# Revit family: НЕВАТОМ_Вентилятор ВР 280-46, Версия 2
name_source: partatom
category: Оборудование
revit_build: Autodesk Revit 2017 (Build: 20170118_1100(x64)
units: mm (PartAtom-declared; Revit-internal decimal feet)

## family parameters
Всегда вертикально = Да
На основе рабочей плоскости = Нет
Общий = Да
При загрузке вырезать с полостями = Нет
Размер круглого соединителя = Использовать диаметр
Тип детали = Нормальный
Точка расчета площади = Нет

## types (7) — shared parameters
ADSK_Количество = 1
ADSK_Количество фаз = 3
ADSK_Количество фаз числовое = 3
ADSK_Напряжение = 380 В
ADSK_Номинальная мощность = 0 Вт
ADSK_Свободный напор воздуха = 0.0 Па
ADSK_Ток = 0 А
l патрубка = 80 мм
НЕВАТОМ_Исполнение вентилятора = 1 мм
ТП = НЕВАТОМ_Вентилятор ВР 240-46

## per-type parameters (varying)
- №2.5: A1=162 мм; AA=175 мм; BB=175 мм; D=250 мм; D внешний=300 мм; D входного патрубка=250 мм; D/2=50 мм; D1=255 мм; H=260 мм; H1=306 мм; L двиг=50 мм; L длина опоры=468 мм; R1=210 мм; R2=180 мм; Type=38 мм; URL=https://t.me; b=20 мм; d двиг=100 мм; h=120 мм; h1=180 мм; h2=155 мм; h3=0 мм; k=50 мм; l двиг=120 мм; l длина=260 мм; r=50 мм; ВР=2.5 мм; НЕВАТОМ_Мощность электродвигатель=0.37 мм; НЕВАТОМ_Направление вращения Левое=Да; НЕВАТОМ_Направление вращения Правое=Нет; НЕВАТОМ_Частота вращения электродвигателя=1500 мм; Ширина опоры=310 мм; Ширина основания=310 мм; с1=260 мм; с2=208 мм
- №3.15: A1=204 мм; AA=220.5 мм; BB=220.5 мм; D=315 мм; D внешний=365 мм; D входного патрубка=315 мм; D/2=50 мм; D1=320 мм; H=325 мм; H1=375 мм; L двиг=50 мм; L длина опоры=527 мм; R1=257 мм; R2=200 мм; Type=39 мм; b=20 мм; d двиг=100 мм; h=120 мм; h1=220 мм; h2=200 мм; h3=100 мм; k=1 мм; l двиг=120 мм; l длина=300 мм; r=50 мм; ВР=3.15 мм; НЕВАТОМ_Мощность электродвигатель=0.55 мм; НЕВАТОМ_Направление вращения Левое=Да; НЕВАТОМ_Направление вращения Правое=Нет; НЕВАТОМ_Частота вращения электродвигателя=1000 мм; Ширина опоры=323 мм; Ширина основания=323 мм; с1=300 мм; с2=227 мм
- №4: A1=260 мм; AA=280 мм; BB=280 мм; D=400 мм; D внешний=450 мм; D входного патрубка=400 мм; D/2=50 мм; D1=405 мм; H=490 мм; H1=541 мм; L двиг=100 мм; L длина опоры=616 мм; R1=326 мм; R2=250 мм; Type=40 мм; b=25 мм; d двиг=100 мм; h=200 мм; h1=270 мм; h2=250 мм; h3=100 мм; k=1 мм; l двиг=80 мм; l длина=300 мм; r=50 мм; ВР=4 мм; НЕВАТОМ_Мощность электродвигатель=1.1 мм; НЕВАТОМ_Направление вращения Левое=Да; НЕВАТОМ_Направление вращения Правое=Нет; НЕВАТОМ_Частота вращения электродвигателя=1000 мм; Ширина опоры=434 мм; Ширина основания=434 мм; с1=300 мм; с2=316 мм
- №5: A1=325 мм; AA=350 мм; BB=350 мм; D=500 мм; D внешний=550 мм; D входного патрубка=500 мм; D/2=50 мм; D1=505 мм; H=600 мм; H1=650 мм; L двиг=100 мм; L длина опоры=860 мм; R1=400 мм; R2=310 мм; Type=41 мм; b=25 мм; d двиг=100 мм; h=150 мм; h1=335 мм; h2=310 мм; h3=100 мм; k=1 мм; l двиг=80 мм; l длина=450 мм; r=50 мм; ВР=5 мм; НЕВАТОМ_Мощность электродвигатель=4 мм; НЕВАТОМ_Направление вращения Левое=Да; НЕВАТОМ_Направление вращения Правое=Нет; НЕВАТОМ_Частота вращения электродвигателя=1000 мм; Ширина опоры=476 мм; Ширина основания=476 мм; с1=450 мм; с2=410 мм
- №6.3: A1=409 мм; AA=441 мм; BB=441 мм; D=630 мм; D внешний=700 мм; D входного патрубка=630 мм; D/2=120 мм; D1=635 мм; H=627 мм; H1=747 мм; L двиг=100 мм; L длина опоры=1060 мм; R1=513 мм; R2=400 мм; Type=41 мм; b=25 мм; d двиг=240 мм; h=300 мм; h1=415 мм; h2=395 мм; h3=100 мм; k=1 мм; l двиг=300 мм; l длина=500 мм; r=120 мм; ВР=6.3 мм; НЕВАТОМ_Мощность электродвигатель=5.5 мм; НЕВАТОМ_Направление вращения Левое=Да; НЕВАТОМ_Направление вращения Правое=Нет; НЕВАТОМ_Частота вращения электродвигателя=750 мм; Ширина опоры=556 мм; Ширина основания=556 мм; с1=500 мм; с2=560 мм
- №8: A1=520 мм; AA=560 мм; BB=560 мм; D=800 мм; D внешний=850 мм; D входного патрубка=800 мм; D/2=200 мм; D1=805 мм; H=700 мм; H1=900 мм; L двиг=300 мм; L длина опоры=1230 мм; R1=650 мм; R2=500 мм; Type=42 мм; b=25 мм; d двиг=400 мм; h=300 мм; h1=540 мм; h2=500 мм; h3=100 мм; k=0 мм; l двиг=300 мм; l длина=600 мм; r=200 мм; ВР=8 мм; НЕВАТОМ_Мощность электродвигатель=15 мм; НЕВАТОМ_Направление вращения Левое=Да; НЕВАТОМ_Направление вращения Правое=Нет; НЕВАТОМ_Частота вращения электродвигателя=750 мм; Ширина опоры=646 мм; Ширина основания=1068 мм; с1=600 мм; с2=630 мм
- №2.0: A1=162 мм; AA=140 мм; BB=140 мм; D=220 мм; D внешний=270 мм; D входного патрубка=220 мм; D/2=50 мм; D1=225 мм; H=220 мм; H1=270 мм; L двиг=50 мм; L длина опоры=378 мм; R1=190 мм; R2=160 мм; Type=38 мм; b=20 мм; d двиг=100 мм; h=120 мм; h1=170 мм; h2=150 мм; h3=0 мм; k=50 мм; l двиг=120 мм; l длина=160 мм; r=50 мм; ВР=2 мм; НЕВАТОМ_Мощность электродвигатель=0.18 мм; НЕВАТОМ_Направление вращения Левое=Нет; НЕВАТОМ_Направление вращения Правое=Да; НЕВАТОМ_Частота вращения электродвигателя=3000 мм; Ширина опоры=325 мм; Ширина основания=325 мм; с1=160 мм; с2=220 мм
